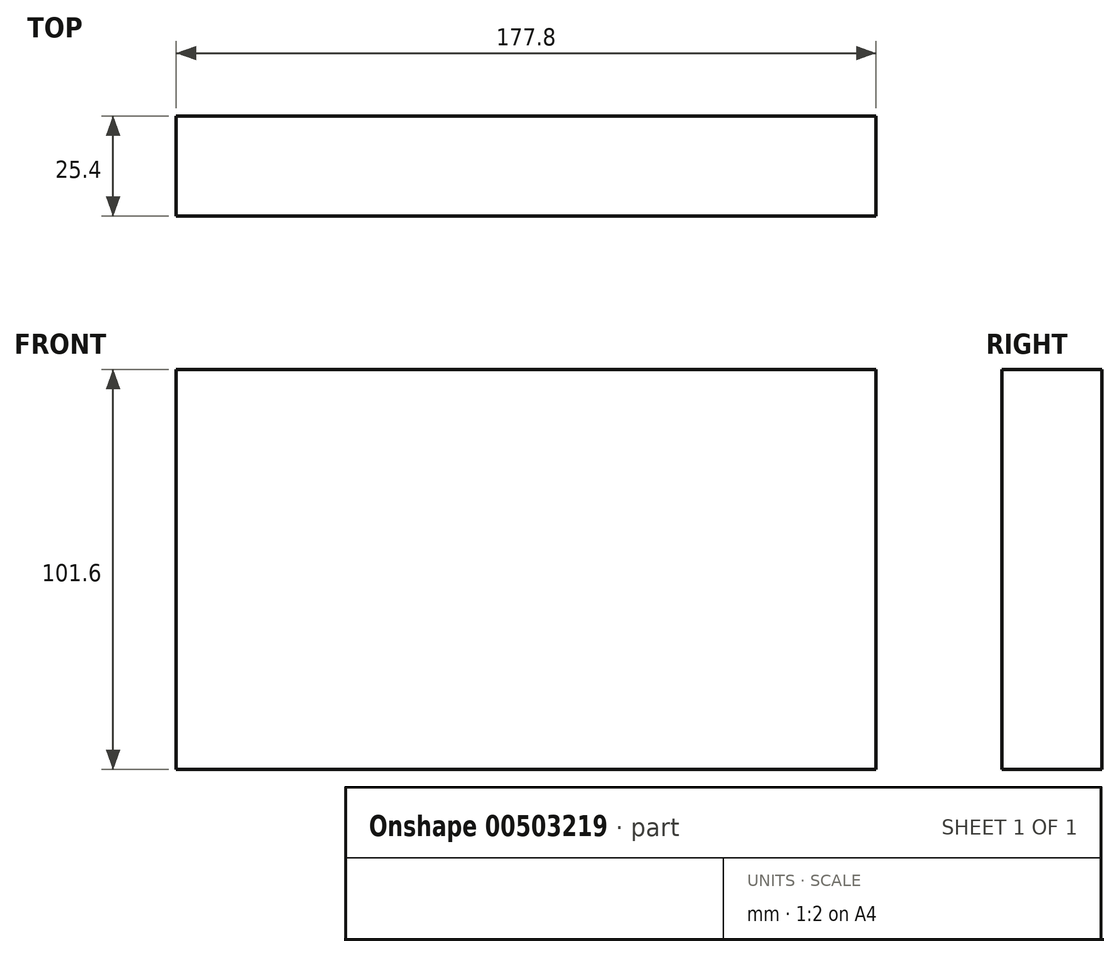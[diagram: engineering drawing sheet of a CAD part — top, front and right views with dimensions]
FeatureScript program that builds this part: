
annotation { "Feature Type Name" : "Feature", "Feature Type Description" : "" }
export const myFeature = defineFeature(function(context is Context, id is Id, definition is map)
    precondition{}
    {
        {
            var Q0;
            Q0=qCreatedBy(makeId("Front.planeOp"),FACE);
            var sketch = newSketch(context, id + "F0", { "sketchPlane" : qUnion([Q0])});
            skLineSegment(sketch, "E0.bottom", {"start": v(-88.9, 50.8) * mm, "end": v(88.9, 50.8) * mm});
            skLineSegment(sketch, "E0.top", {"start": v(-88.9, -50.8) * mm, "end": v(88.9, -50.8) * mm});
            skLineSegment(sketch, "E0.left", {"start": v(-88.9, 50.8) * mm, "end": v(-88.9, -50.8) * mm});
            skLineSegment(sketch, "E0.right", {"start": v(88.9, 50.8) * mm, "end": v(88.9, -50.8) * mm});
            skPoint(sketch, "E0.middle", {"position": v(0, 0) * mm});
            skSolve(sketch);
        }
        {
            var Q0;
            Q0 = qSketchRegion(id + "F0", true);
            extrude(context, id + "F1", {"entities" : qUnion([Q0]), "endBound" : BoundingType.SYMMETRIC, "depth" : 25.4 * mm});
        }
    });
